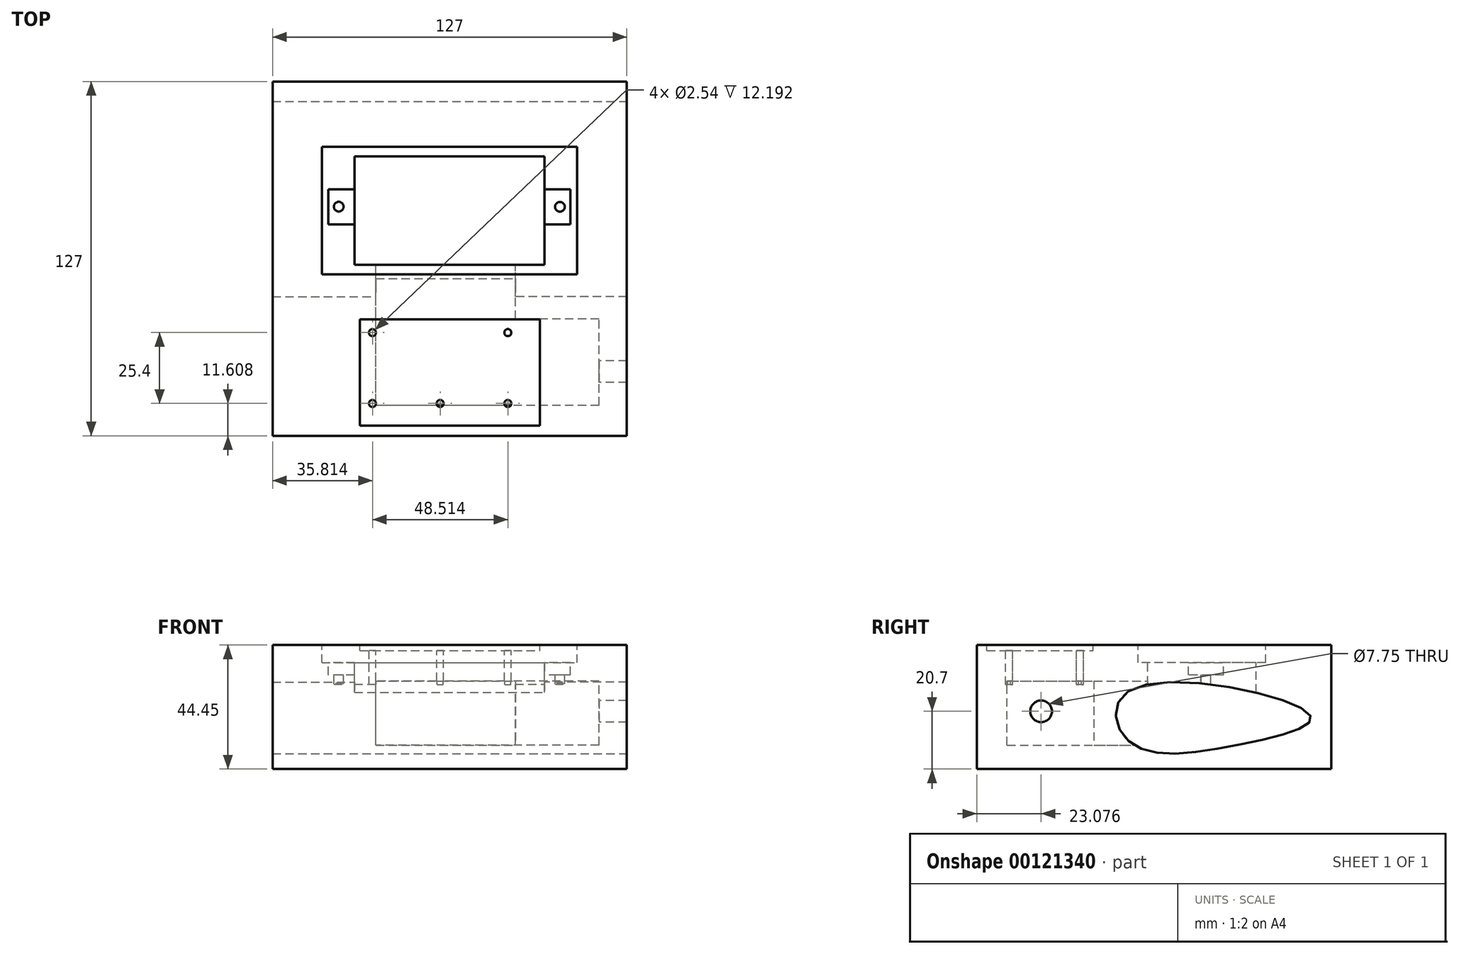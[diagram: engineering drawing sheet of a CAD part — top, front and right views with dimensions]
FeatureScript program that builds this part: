
annotation { "Feature Type Name" : "Feature", "Feature Type Description" : "" }
export const myFeature = defineFeature(function(context is Context, id is Id, definition is map)
    precondition{}
    {
        {
            var Q0;
            Q0=qCreatedBy(makeId("Top.planeOp"),FACE);
            var sketch = newSketch(context, id + "F0", { "sketchPlane" : qUnion([Q0])});
            skLineSegment(sketch, "E0.bottom", {"start": v(63.5, 63.5) * mm, "end": v(-63.5, 63.5) * mm});
            skLineSegment(sketch, "E0.top", {"start": v(63.5, -63.5) * mm, "end": v(-63.5, -63.5) * mm});
            skLineSegment(sketch, "E0.left", {"start": v(63.5, 63.5) * mm, "end": v(63.5, -63.5) * mm});
            skLineSegment(sketch, "E0.right", {"start": v(-63.5, 63.5) * mm, "end": v(-63.5, -63.5) * mm});
            skPoint(sketch, "E0.middle", {"position": v(0, 0) * mm});
            skSolve(sketch);
        }
        {
            var Q0;
            Q0 = qSketchRegion(id + "F0", true);
            extrude(context, id + "F1", {"entities" : qUnion([Q0]), "depth" : 44.45 * mm});
        }
        {
            var Q0;
            Q0=makeQuery(id+"F1.opExtrude","CAP_FACE",FACE,{"disambiguationData":[OSD([sQuery(id+"F0.wireOp",EDGE,"E0.bottom"),sQuery(id+"F0.wireOp",EDGE,"E0.top"),sQuery(id+"F0.wireOp",EDGE,"E0.left"),sQuery(id+"F0.wireOp",EDGE,"E0.right")])],"isStart":false});
            var sketch = newSketch(context, id + "F2", { "sketchPlane" : qUnion([Q0])});
            skLineSegment(sketch, "E1.bottom", {"start": v(-32.26, -59.9) * mm, "end": v(32.26, -59.9) * mm});
            skLineSegment(sketch, "E1.top", {"start": v(-32.26, -21.8) * mm, "end": v(32.26, -21.8) * mm});
            skLineSegment(sketch, "E1.left", {"start": v(-32.26, -59.9) * mm, "end": v(-32.26, -21.8) * mm});
            skLineSegment(sketch, "E1.right", {"start": v(32.26, -59.9) * mm, "end": v(32.26, -21.8) * mm});
            skSolve(sketch);
        }
        {
            var Q0;
            Q0 = qSketchRegion(id + "F2", true);
            extrude(context, id + "F3", {"entities" : qUnion([Q0]), "operationType" : NewBodyOperationType.REMOVE, "oppositeDirection" : true, "depth" : 2.03 * mm});
        }
        {
            var Q0;
            Q0=makeQuery(id+"F3.boolean.opBoolean","COPY",FACE,{"derivedFrom":makeQuery(id+"F3.opExtrude","CAP_FACE",FACE,{"disambiguationData":[OSD([sQuery(id+"F2.wireOp",EDGE,"E1.bottom"),sQuery(id+"F2.wireOp",EDGE,"E1.top"),sQuery(id+"F2.wireOp",EDGE,"E1.left"),sQuery(id+"F2.wireOp",EDGE,"E1.right")])],"isStart":false})});
            var sketch = newSketch(context, id + "F4", { "sketchPlane" : qUnion([Q0])});
            skCircle(sketch, "E2", {"center": v(20.83, -26.5) * mm, "radius": 1.27 * mm});
            skCircle(sketch, "E3.0.1.0", {"center": v(20.83, -51.9) * mm, "radius": 1.27 * mm});
            skCircle(sketch, "E3.1.0.0", {"center": v(-3.43, -26.5) * mm, "radius": 1.27 * mm});
            skCircle(sketch, "E3.1.1.0", {"center": v(-3.43, -51.9) * mm, "radius": 1.27 * mm});
            skCircle(sketch, "E3.2.0.0", {"center": v(-27.69, -26.5) * mm, "radius": 1.27 * mm});
            skCircle(sketch, "E3.2.1.0", {"center": v(-27.69, -51.9) * mm, "radius": 1.27 * mm});
            skLineSegment(sketch, "E3.direction1", {"start": v(20.83, -26.5) * mm, "end": v(-3.43, -26.5) * mm, "construction": true});
            skLineSegment(sketch, "E3.direction2", {"start": v(20.83, -26.5) * mm, "end": v(20.83, -51.9) * mm, "construction": true});
            skSolve(sketch);
        }
        {
            var Q0;
            Q0=makeQuery(id+"F4.imprint","IMPRINT",FACE,{"disambiguationData":[TD([[makeQuery(id+"F4.imprint","IMPRINT",EDGE,{"derivedFrom":sQuery(id+"F4.wireOp",EDGE,"E2")}),1.0]])]});
            var Q1;
            Q1=makeQuery(id+"F4.imprint","IMPRINT",FACE,{"disambiguationData":[TD([[makeQuery(id+"F4.imprint","IMPRINT",EDGE,{"derivedFrom":sQuery(id+"F4.wireOp",EDGE,"E3.0.1.0")}),1.0]])]});
            var Q2;
            Q2=makeQuery(id+"F4.imprint","IMPRINT",FACE,{"disambiguationData":[TD([[makeQuery(id+"F4.imprint","IMPRINT",EDGE,{"derivedFrom":sQuery(id+"F4.wireOp",EDGE,"E3.1.1.0")}),1.0]])]});
            var Q3;
            Q3=makeQuery(id+"F4.imprint","IMPRINT",FACE,{"disambiguationData":[TD([[makeQuery(id+"F4.imprint","IMPRINT",EDGE,{"derivedFrom":sQuery(id+"F4.wireOp",EDGE,"E3.1.0.0")}),1.0]])]});
            var Q4;
            Q4=makeQuery(id+"F4.imprint","IMPRINT",FACE,{"disambiguationData":[TD([[makeQuery(id+"F4.imprint","IMPRINT",EDGE,{"derivedFrom":sQuery(id+"F4.wireOp",EDGE,"E3.2.0.0")}),1.0]])]});
            var Q5;
            Q5=makeQuery(id+"F4.imprint","IMPRINT",FACE,{"disambiguationData":[TD([[makeQuery(id+"F4.imprint","IMPRINT",EDGE,{"derivedFrom":sQuery(id+"F4.wireOp",EDGE,"E3.2.1.0")}),1.0]])]});
            extrude(context, id + "F5", {"entities" : qUnion([Q0, Q1, Q2, Q3, Q4, Q5]), "operationType" : NewBodyOperationType.REMOVE, "oppositeDirection" : true, "depth" : 12.2 * mm});
        }
        {
            var Q0;
            Q0=makeQuery(id+"F5.boolean.opBoolean","COPY",FACE,{"derivedFrom":makeQuery(id+"F5.opExtrude","CAP_FACE",FACE,{"disambiguationData":[OSD([sQuery(id+"F4.wireOp",EDGE,"E3.1.0.0")])],"isStart":false})});
            var sketch = newSketch(context, id + "F6", { "sketchPlane" : qUnion([Q0])});
            skSolve(sketch);
        }
        {
            var Q0;
            Q0=makeQuery(id+"F6.imprint","IMPRINT",FACE,{"disambiguationData":[TD([[makeQuery(id+"F6.imprint","IMPRINT",EDGE,{"derivedFrom":makeQuery(id+"F5.boolean.opBoolean","COPY",EDGE,{"derivedFrom":makeQuery(id+"F5.opExtrude","CAP_EDGE",EDGE,{"disambiguationData":[OSD([sQuery(id+"F4.wireOp",EDGE,"E3.1.0.0")])],"isStart":false})})}),1.0]])]});
            var Q1;
            Q1=makeQuery(id+"F3.boolean.opBoolean","COPY",FACE,{"derivedFrom":makeQuery(id+"F3.opExtrude","CAP_FACE",FACE,{"disambiguationData":[OSD([sQuery(id+"F2.wireOp",EDGE,"E1.bottom"),sQuery(id+"F2.wireOp",EDGE,"E1.top"),sQuery(id+"F2.wireOp",EDGE,"E1.left"),sQuery(id+"F2.wireOp",EDGE,"E1.right")])],"isStart":false})});
            extrude(context, id + "F7", {"entities" : qUnion([Q0]), "operationType" : NewBodyOperationType.ADD, "endBound" : BoundingType.UP_TO_SURFACE, "endBoundEntityFace" : qUnion([Q1]), "depth" : 25.4 * mm});
        }
        {
            var Q0;
            Q0=makeQuery(id+"F1.opExtrude","SWEPT_FACE",FACE,{"disambiguationData":[OSD([sQuery(id+"F0.wireOp",EDGE,"E0.left")])]});
            var sketch = newSketch(context, id + "F8", { "sketchPlane" : qUnion([Q0])});
            skFitSpline(sketch, "E4", {"points": [v(-9.1, 10.08) * mm, v(-8.68, 28.2) * mm, v(55.9, 19.42) * mm, v(32.6, 9.18) * mm, v(-9.1, 10.08) * mm]});
            skSolve(sketch);
        }
        {
            var Q0;
            Q0 = qSketchRegion(id + "F8", true);
            var Q1;
            Q1=makeQuery(id+"F1.opExtrude","SWEPT_FACE",FACE,{"disambiguationData":[OSD([sQuery(id+"F0.wireOp",EDGE,"E0.right")])]});
            extrude(context, id + "F9", {"entities" : qUnion([Q0]), "operationType" : NewBodyOperationType.REMOVE, "endBound" : BoundingType.UP_TO_SURFACE, "oppositeDirection" : true, "endBoundEntityFace" : qUnion([Q1]), "depth" : 25.4 * mm});
        }
        {
            var Q0;
            Q0=makeQuery(id+"F1.opExtrude","CAP_FACE",FACE,{"disambiguationData":[OSD([sQuery(id+"F0.wireOp",EDGE,"E0.bottom"),sQuery(id+"F0.wireOp",EDGE,"E0.top"),sQuery(id+"F0.wireOp",EDGE,"E0.left"),sQuery(id+"F0.wireOp",EDGE,"E0.right")])],"isStart":false});
            var sketch = newSketch(context, id + "F10", { "sketchPlane" : qUnion([Q0])});
            skLineSegment(sketch, "E5", {"start": v(37.1, -5.66) * mm, "end": v(-54.85, -5.66) * mm, "construction": true});
            skLineSegment(sketch, "E6", {"start": v(-45.81, -5.66) * mm, "end": v(45.63, -5.66) * mm});
            skLineSegment(sketch, "E7", {"start": v(45.63, -5.66) * mm, "end": v(45.63, 40.06) * mm});
            skLineSegment(sketch, "E8", {"start": v(45.63, 40.06) * mm, "end": v(-45.81, 40.06) * mm});
            skLineSegment(sketch, "E9", {"start": v(-45.81, 40.06) * mm, "end": v(-45.81, -5.66) * mm});
            skSolve(sketch);
        }
        {
            var Q0;
            Q0 = qSketchRegion(id + "F10", true);
            extrude(context, id + "F11", {"entities" : qUnion([Q0]), "operationType" : NewBodyOperationType.REMOVE, "oppositeDirection" : true, "depth" : 6.35 * mm});
        }
        {
            var Q0;
            Q0=makeQuery(id+"F11.boolean.opBoolean","COPY",FACE,{"derivedFrom":makeQuery(id+"F11.opExtrude","CAP_FACE",FACE,{"disambiguationData":[OSD([sQuery(id+"F10.wireOp",EDGE,"E6"),sQuery(id+"F10.wireOp",EDGE,"E7"),sQuery(id+"F10.wireOp",EDGE,"E8"),sQuery(id+"F10.wireOp",EDGE,"E9")])],"isStart":false})});
            var sketch = newSketch(context, id + "F12", { "sketchPlane" : qUnion([Q0])});
            skLineSegment(sketch, "E10.bottom", {"start": v(-34.16, 36.66) * mm, "end": v(33.91, 36.66) * mm});
            skLineSegment(sketch, "E10.top", {"start": v(-34.16, -2.21) * mm, "end": v(33.91, -2.21) * mm});
            skLineSegment(sketch, "E10.left", {"start": v(-34.16, 36.66) * mm, "end": v(-34.16, -2.21) * mm});
            skLineSegment(sketch, "E10.right", {"start": v(33.91, 36.66) * mm, "end": v(33.91, -2.21) * mm});
            skSolve(sketch);
        }
        {
            var Q0;
            Q0 = qSketchRegion(id + "F12", true);
            extrude(context, id + "F13", {"entities" : qUnion([Q0]), "operationType" : NewBodyOperationType.REMOVE, "oppositeDirection" : true, "depth" : 13.87 * mm});
        }
        {
            var Q0;
            Q0=makeQuery(id+"F11.boolean.opBoolean","COPY",FACE,{"derivedFrom":makeQuery(id+"F11.opExtrude","CAP_FACE",FACE,{"disambiguationData":[OSD([sQuery(id+"F10.wireOp",EDGE,"E6"),sQuery(id+"F10.wireOp",EDGE,"E7"),sQuery(id+"F10.wireOp",EDGE,"E8"),sQuery(id+"F10.wireOp",EDGE,"E9")])],"isStart":false})});
            var sketch = newSketch(context, id + "F14", { "sketchPlane" : qUnion([Q0])});
            skLineSegment(sketch, "E11.bottom", {"start": v(-34.16, 12.35) * mm, "end": v(-43.51, 12.35) * mm});
            skLineSegment(sketch, "E11.top", {"start": v(-34.16, 24.89) * mm, "end": v(-43.51, 24.89) * mm});
            skLineSegment(sketch, "E11.left", {"start": v(-34.16, 12.35) * mm, "end": v(-34.16, 24.89) * mm});
            skLineSegment(sketch, "E11.right", {"start": v(-43.51, 12.35) * mm, "end": v(-43.51, 24.89) * mm});
            skLineSegment(sketch, "E12.1.0.0", {"start": v(43.24, 24.89) * mm, "end": v(33.89, 24.89) * mm});
            skLineSegment(sketch, "E12.1.0.1", {"start": v(33.89, 12.35) * mm, "end": v(33.89, 24.89) * mm});
            skLineSegment(sketch, "E12.1.0.2", {"start": v(43.24, 12.35) * mm, "end": v(33.89, 12.35) * mm});
            skLineSegment(sketch, "E12.1.0.3", {"start": v(43.24, 12.35) * mm, "end": v(43.24, 24.89) * mm});
            skLineSegment(sketch, "E12.direction1", {"start": v(-43.51, 24.89) * mm, "end": v(33.89, 24.89) * mm, "construction": true});
            skSolve(sketch);
        }
        {
            var Q0;
            Q0 = qSketchRegion(id + "F14", true);
            extrude(context, id + "F15", {"entities" : qUnion([Q0]), "operationType" : NewBodyOperationType.REMOVE, "oppositeDirection" : true, "depth" : 4.4 * mm});
        }
        {
            var Q0;
            Q0=makeQuery(id+"F15.boolean.opBoolean","COPY",FACE,{"derivedFrom":makeQuery(id+"F15.opExtrude","CAP_FACE",FACE,{"disambiguationData":[OSD([sQuery(id+"F14.wireOp",EDGE,"E11.bottom"),sQuery(id+"F14.wireOp",EDGE,"E11.top"),sQuery(id+"F14.wireOp",EDGE,"E11.left"),sQuery(id+"F14.wireOp",EDGE,"E11.right")])],"isStart":false})});
            var sketch = newSketch(context, id + "F16", { "sketchPlane" : qUnion([Q0])});
            skCircle(sketch, "E13", {"center": v(-39.77, 18.66) * mm, "radius": 1.74 * mm});
            skCircle(sketch, "E14", {"center": v(39.5, 18.62) * mm, "radius": 1.74 * mm});
            skPoint(sketch, "E14.centerSnap0", {"position": v(-34.16, 18.62) * mm});
            skSolve(sketch);
        }
        {
            var Q0;
            Q0=makeQuery(id+"F16.imprint","IMPRINT",FACE,{"disambiguationData":[TD([[makeQuery(id+"F16.imprint","IMPRINT",EDGE,{"derivedFrom":sQuery(id+"F16.wireOp",EDGE,"E14")}),1.0]])]});
            var Q1;
            Q1=makeQuery(id+"F16.imprint","IMPRINT",FACE,{"disambiguationData":[TD([[makeQuery(id+"F16.imprint","IMPRINT",EDGE,{"derivedFrom":sQuery(id+"F16.wireOp",EDGE,"E13")}),1.0]])]});
            extrude(context, id + "F17", {"entities" : qUnion([Q0, Q1]), "operationType" : NewBodyOperationType.REMOVE, "oppositeDirection" : true, "depth" : 8.4 * mm});
        }
        {
            var Q0;
            Q0=qCreatedBy(makeId("Front.planeOp"),FACE);
            var sketch = newSketch(context, id + "F18", { "sketchPlane" : qUnion([Q0])});
            skLineSegment(sketch, "E15.bottom", {"start": v(23.5, 8.59) * mm, "end": v(-26.5, 8.59) * mm});
            skLineSegment(sketch, "E15.top", {"start": v(23.5, 31.59) * mm, "end": v(-26.5, 31.59) * mm});
            skLineSegment(sketch, "E15.left", {"start": v(23.5, 8.59) * mm, "end": v(23.5, 31.59) * mm});
            skLineSegment(sketch, "E15.right", {"start": v(-26.5, 8.59) * mm, "end": v(-26.5, 31.59) * mm});
            skSolve(sketch);
        }
        {
            var Q0;
            Q0 = qSketchRegion(id + "F18", true);
            extrude(context, id + "F19", {"entities" : qUnion([Q0]), "operationType" : NewBodyOperationType.REMOVE, "depth" : 52.6 * mm});
        }
        {
            var Q0;
            Q0=makeQuery(id+"F19.boolean.opBoolean","COPY",FACE,{"derivedFrom":makeQuery(id+"F19.opExtrude","SWEPT_FACE",FACE,{"disambiguationData":[OSD([sQuery(id+"F18.wireOp",EDGE,"E15.left")])]})});
            var sketch = newSketch(context, id + "F20", { "sketchPlane" : qUnion([Q0])});
            skLineSegment(sketch, "E16.bottom", {"start": v(21.6, 31.59) * mm, "end": v(52.6, 31.59) * mm});
            skLineSegment(sketch, "E16.top", {"start": v(21.6, 8.59) * mm, "end": v(52.6, 8.59) * mm});
            skLineSegment(sketch, "E16.left", {"start": v(21.6, 31.59) * mm, "end": v(21.6, 8.59) * mm});
            skLineSegment(sketch, "E16.right", {"start": v(52.6, 31.59) * mm, "end": v(52.6, 8.59) * mm});
            skSolve(sketch);
        }
        {
            var Q0;
            Q0 = qSketchRegion(id + "F20", true);
            extrude(context, id + "F21", {"entities" : qUnion([Q0]), "operationType" : NewBodyOperationType.REMOVE, "oppositeDirection" : true, "depth" : 30 * mm});
        }
        {
            var Q0;
            Q0=makeQuery(id+"F21.boolean.opBoolean","COPY",FACE,{"derivedFrom":makeQuery(id+"F21.opExtrude","CAP_FACE",FACE,{"disambiguationData":[OSD([sQuery(id+"F20.wireOp",EDGE,"E16.bottom"),sQuery(id+"F20.wireOp",EDGE,"E16.top"),sQuery(id+"F20.wireOp",EDGE,"E16.left"),sQuery(id+"F20.wireOp",EDGE,"E16.right")])],"isStart":false})});
            var sketch = newSketch(context, id + "F22", { "sketchPlane" : qUnion([Q0])});
            skCircle(sketch, "E17", {"center": v(40.42, 20.7) * mm, "radius": 3.88 * mm});
            skSolve(sketch);
        }
        {
            var Q0;
            Q0 = qSketchRegion(id + "F22", true);
            extrude(context, id + "F23", {"entities" : qUnion([Q0]), "operationType" : NewBodyOperationType.REMOVE, "oppositeDirection" : true, "depth" : 10.4 * mm});
        }
    });
